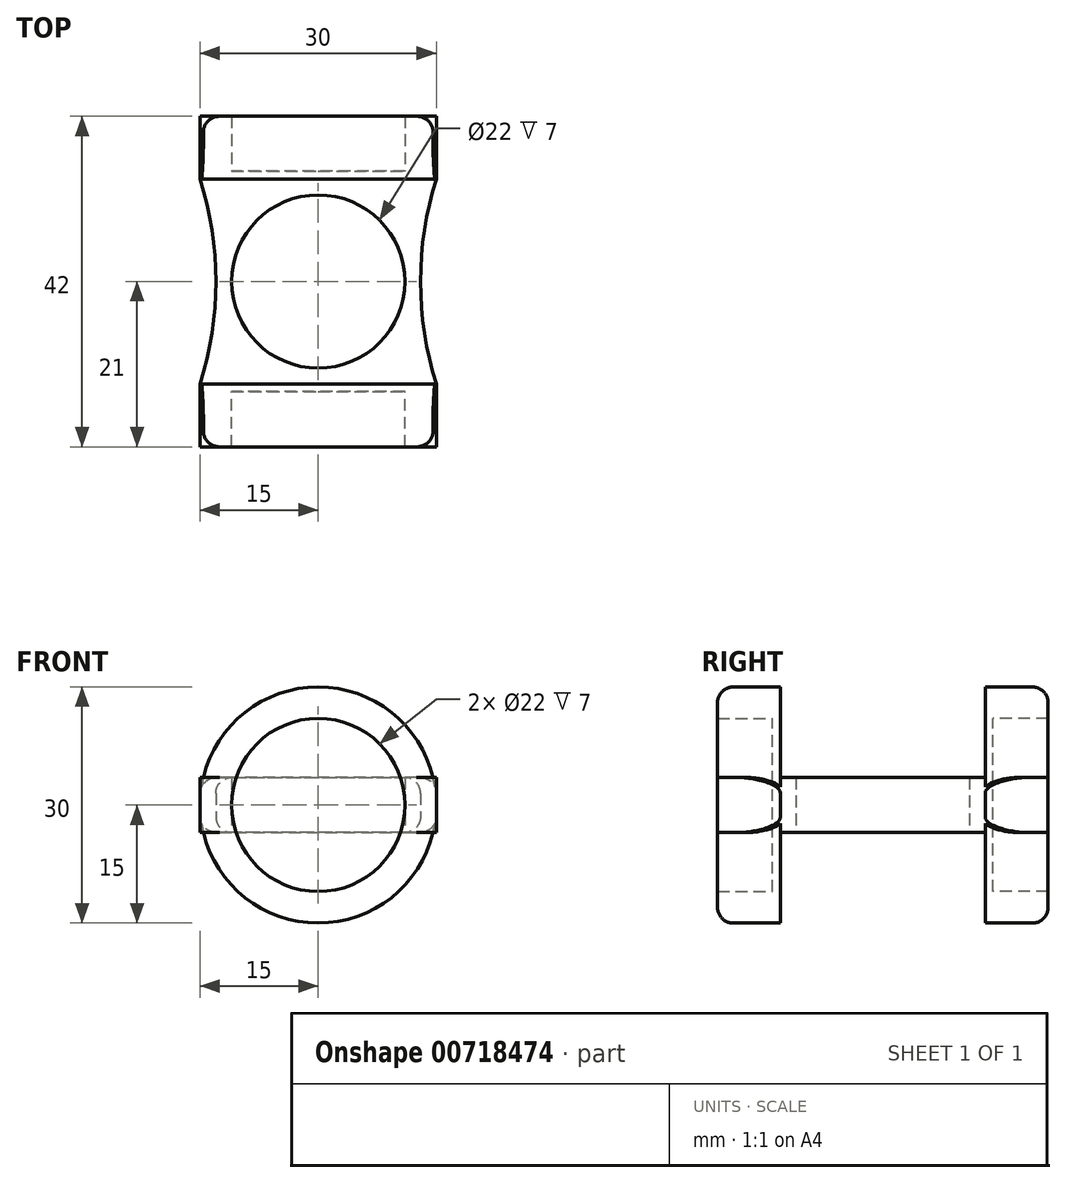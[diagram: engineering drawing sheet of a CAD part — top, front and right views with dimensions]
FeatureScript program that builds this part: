
annotation { "Feature Type Name" : "Feature", "Feature Type Description" : "" }
export const myFeature = defineFeature(function(context is Context, id is Id, definition is map)
    precondition{}
    {
        {
            var Q0;
            Q0=qCreatedBy(makeId("Top.planeOp"),FACE);
            var sketch = newSketch(context, id + "F0", { "sketchPlane" : qUnion([Q0])});
            skCircle(sketch, "E0", {"center": v(0, 0) * mm, "radius": 11 * mm});
            skArc(sketch, "E1.0", {"start": v(7.48, 13) * mm, "mid": v(-4.41, 14.34) * mm, "end": v(-13.5, 6.54) * mm});
            skLineSegment(sketch, "E2", {"start": v(0, 11) * mm, "end": v(0, 15) * mm});
            skLineSegment(sketch, "E3", {"start": v(0, 13) * mm, "end": v(15, 13) * mm});
            skLineSegment(sketch, "E4.MirrorCS", {"start": v(0, 13) * mm, "end": v(-15, 13) * mm});
            skLineSegment(sketch, "E5.MirrorCS", {"start": v(0, -13) * mm, "end": v(15, -13) * mm});
            skLineSegment(sketch, "E6.MirrorCS", {"start": v(0, -13) * mm, "end": v(-15, -13) * mm});
            skPoint(sketch, "E7", {"position": v(13, 0) * mm});
            skArc(sketch, "E8", {"start": v(15, 13) * mm, "mid": v(13, 0) * mm, "end": v(15, -13) * mm});
            skArc(sketch, "E9.MirrorCS", {"start": v(-15, 13) * mm, "mid": v(-13, 0) * mm, "end": v(-15, -13) * mm});
            skArc(sketch, "E10.trimOffspring", {"start": v(-13.5, -6.54) * mm, "mid": v(-4.41, -14.34) * mm, "end": v(7.48, -13) * mm});
            skSolve(sketch);
        }
        {
            var Q0;
            Q0=qCreatedBy(makeId("Front.planeOp"),FACE);
            cPlane(context, id + "F1", {"entities" : qUnion([Q0]), "cplaneType" : CPlaneType.OFFSET, "offset" : 13 * mm, "width" : 150 * mm, "height" : 150 * mm});
        }
        {
            var Q0;
            Q0=qCreatedBy(makeId("Front.planeOp"),FACE);
            cPlane(context, id + "F2", {"entities" : qUnion([Q0]), "cplaneType" : CPlaneType.OFFSET, "offset" : 13 * mm, "oppositeDirection" : true, "width" : 150 * mm, "height" : 150 * mm});
        }
        {
            var Q0;
            Q0=qCreatedBy(id+"F1.planeOp",FACE);
            var sketch = newSketch(context, id + "F3", { "sketchPlane" : qUnion([Q0])});
            skCircle(sketch, "E11", {"center": v(0, 0) * mm, "radius": 11 * mm});
            skCircle(sketch, "E12.0", {"center": v(0, 0) * mm, "radius": 15 * mm});
            skLineSegment(sketch, "E13", {"start": v(15, 0) * mm, "end": v(15, 3.5) * mm});
            skLineSegment(sketch, "E14", {"start": v(15, 3.5) * mm, "end": v(14.59, 3.5) * mm});
            skLineSegment(sketch, "E15.MirrorCS", {"start": v(15, 0) * mm, "end": v(15, -3.5) * mm});
            skLineSegment(sketch, "E16.MirrorCS", {"start": v(15, -3.5) * mm, "end": v(14.59, -3.5) * mm});
            skLineSegment(sketch, "E17.MirrorCS", {"start": v(-15, 0) * mm, "end": v(-15, 3.5) * mm});
            skLineSegment(sketch, "E18.MirrorCS", {"start": v(-15, 3.5) * mm, "end": v(-14.59, 3.5) * mm});
            skLineSegment(sketch, "E19.MirrorCS", {"start": v(-15, 0) * mm, "end": v(-15, -3.5) * mm});
            skLineSegment(sketch, "E20.MirrorCS", {"start": v(-15, -3.5) * mm, "end": v(-14.59, -3.5) * mm});
            skSolve(sketch);
        }
        {
            var Q0;
            Q0=qCreatedBy(id+"F2.planeOp",FACE);
            var sketch = newSketch(context, id + "F4", { "sketchPlane" : qUnion([Q0])});
            skCircle(sketch, "E21", {"center": v(0, 0) * mm, "radius": 11 * mm});
            skCircle(sketch, "E22.0", {"center": v(0, 0) * mm, "radius": 15 * mm});
            skLineSegment(sketch, "E23", {"start": v(-15, 0) * mm, "end": v(-15, 3.5) * mm});
            skLineSegment(sketch, "E24", {"start": v(-15, 3.5) * mm, "end": v(-14.59, 3.5) * mm});
            skLineSegment(sketch, "E25.MirrorCS", {"start": v(-15, 0) * mm, "end": v(-15, -3.5) * mm});
            skLineSegment(sketch, "E26.MirrorCS", {"start": v(-15, -3.5) * mm, "end": v(-14.59, -3.5) * mm});
            skLineSegment(sketch, "E27.MirrorCS", {"start": v(15, 0) * mm, "end": v(15, -3.5) * mm});
            skLineSegment(sketch, "E28.MirrorCS", {"start": v(15, -3.5) * mm, "end": v(14.59, -3.5) * mm});
            skLineSegment(sketch, "E29.MirrorCS", {"start": v(15, 0) * mm, "end": v(15, 3.5) * mm});
            skLineSegment(sketch, "E30.MirrorCS", {"start": v(15, 3.5) * mm, "end": v(14.59, 3.5) * mm});
            skSolve(sketch);
        }
        {
            var Q0;
            Q0 = qSketchRegion(id + "F4", true);
            extrude(context, id + "F5", {"entities" : qUnion([Q0]), "oppositeDirection" : true, "depth" : 8 * mm, "offsetDistance" : 25 * mm});
        }
        {
            var Q0;
            Q0=makeQuery(id+"F4.imprint","IMPRINT",FACE,{"disambiguationData":[TD([[makeQuery(id+"F4.imprint","IMPRINT",EDGE,{"derivedFrom":sQuery(id+"F4.wireOp",EDGE,"E21")}),1.0]])]});
            extrude(context, id + "F6", {"entities" : qUnion([Q0]), "operationType" : NewBodyOperationType.ADD, "oppositeDirection" : true, "depth" : 1 * mm, "offsetDistance" : 25 * mm});
        }
        {
            var Q0;
            Q0=makeQuery(id+"F0.imprint","IMPRINT",FACE,{"disambiguationData":[TD([[makeQuery(id+"F0.imprint","IMPRINT",EDGE,{"derivedFrom":sQuery(id+"F0.wireOp",EDGE,"E0")}),-1.0]])]});
            var Q1;
            {var subQ0=sQuery(id+"F0.wireOp",EDGE,"E9.MirrorCS");var subQ1=sQuery(id+"F0.wireOp",EDGE,"E1.0");var subQ2=makeQuery(id+"F0.imprint","INTERSECT",VERTEX,{"derivedFrom":[subQ1,subQ0]});Q1=makeQuery(id+"F0.imprint","IMPRINT",FACE,{"disambiguationData":[TD([[makeQuery(id+"F0.imprint","IMPRINT",EDGE,{"disambiguationData":[TD([[subQ2,1.0]])],"derivedFrom":subQ1}),-1.0]])]});}
            var Q2;
            {var subQ0=sQuery(id+"F0.wireOp",EDGE,"E9.MirrorCS");var subQ1=sQuery(id+"F0.wireOp",EDGE,"E6.MirrorCS");var subQ2=makeQuery(id+"F0.imprint","INTERSECT",VERTEX,{"derivedFrom":[subQ1,subQ0]});Q2=makeQuery(id+"F0.imprint","IMPRINT",FACE,{"disambiguationData":[TD([[makeQuery(id+"F0.imprint","IMPRINT",EDGE,{"disambiguationData":[TD([[subQ2,1.0]])],"derivedFrom":subQ1}),-1.0]])]});}
            extrude(context, id + "F7", {"entities" : qUnion([Q0, Q1, Q2]), "operationType" : NewBodyOperationType.ADD, "endBound" : BoundingType.SYMMETRIC, "depth" : 7 * mm, "offsetDistance" : 25 * mm});
        }
        {
            var Q0;
            Q0=makeQuery(id+"F3.imprint","IMPRINT",FACE,{"disambiguationData":[TD([[makeQuery(id+"F3.imprint","IMPRINT",EDGE,{"derivedFrom":sQuery(id+"F3.wireOp",EDGE,"E11")}),1.0]])]});
            extrude(context, id + "F8", {"entities" : qUnion([Q0]), "operationType" : NewBodyOperationType.ADD, "depth" : 1 * mm, "offsetDistance" : 25 * mm});
        }
        {
            var Q0;
            Q0=makeQuery(id+"F3.imprint","IMPRINT",FACE,{"disambiguationData":[TD([[makeQuery(id+"F3.imprint","IMPRINT",EDGE,{"derivedFrom":sQuery(id+"F3.wireOp",EDGE,"E11")}),-1.0]])]});
            var Q1;
            {var subQ0=sQuery(id+"F3.wireOp",EDGE,"E19.MirrorCS");Q1=makeQuery(id+"F3.imprint","IMPRINT",FACE,{"disambiguationData":[TD([[makeQuery(id+"F3.imprint","IMPRINT",EDGE,{"derivedFrom":subQ0}),1.0]])]});}
            var Q2;
            {var subQ0=sQuery(id+"F3.wireOp",EDGE,"E17.MirrorCS");Q2=makeQuery(id+"F3.imprint","IMPRINT",FACE,{"disambiguationData":[TD([[makeQuery(id+"F3.imprint","IMPRINT",EDGE,{"derivedFrom":subQ0}),-1.0]])]});}
            var Q3;
            {var subQ0=sQuery(id+"F3.wireOp",EDGE,"E15.MirrorCS");Q3=makeQuery(id+"F3.imprint","IMPRINT",FACE,{"disambiguationData":[TD([[makeQuery(id+"F3.imprint","IMPRINT",EDGE,{"derivedFrom":subQ0}),-1.0]])]});}
            var Q4;
            {var subQ0=sQuery(id+"F3.wireOp",EDGE,"E13");Q4=makeQuery(id+"F3.imprint","IMPRINT",FACE,{"disambiguationData":[TD([[makeQuery(id+"F3.imprint","IMPRINT",EDGE,{"derivedFrom":subQ0}),1.0]])]});}
            extrude(context, id + "F9", {"entities" : qUnion([Q0, Q1, Q2, Q3, Q4]), "operationType" : NewBodyOperationType.ADD, "depth" : 8 * mm, "offsetDistance" : 25 * mm});
        }
        {
            var Q0;
            Q0=makeQuery(id+"F5.opExtrude","CAP_EDGE",EDGE,{"disambiguationData":[OSD([sQuery(id+"F4.wireOp",EDGE,"E22.0")])],"isStart":false});
            var Q1;
            Q1=makeQuery(id+"F7.opExtrude","CAP_EDGE",EDGE,{"disambiguationData":[OSD([sQuery(id+"F0.wireOp",EDGE,"E9.MirrorCS")])],"isStart":false});
            var Q2;
            Q2=makeQuery(id+"F7.opExtrude","CAP_EDGE",EDGE,{"disambiguationData":[OSD([sQuery(id+"F0.wireOp",EDGE,"E9.MirrorCS")])],"isStart":true});
            var Q3;
            Q3=makeQuery(id+"F7.opExtrude","CAP_EDGE",EDGE,{"disambiguationData":[OSD([sQuery(id+"F0.wireOp",EDGE,"E8")])],"isStart":false});
            var Q4;
            Q4=makeQuery(id+"F7.opExtrude","CAP_EDGE",EDGE,{"disambiguationData":[OSD([sQuery(id+"F0.wireOp",EDGE,"E8")])],"isStart":true});
            var Q5;
            Q5=makeQuery(id+"F9.opExtrude","CAP_EDGE",EDGE,{"disambiguationData":[OSD([sQuery(id+"F3.wireOp",EDGE,"E12.0")])],"isStart":false});
            fillet(context, id + "F10", {"entities" : qUnion([Q0, Q1, Q2, Q3, Q4, Q5]), "radius" : 2 * mm, "tangentPropagation" : true, "allowEdgeOverflow" : false});
        }
    });
